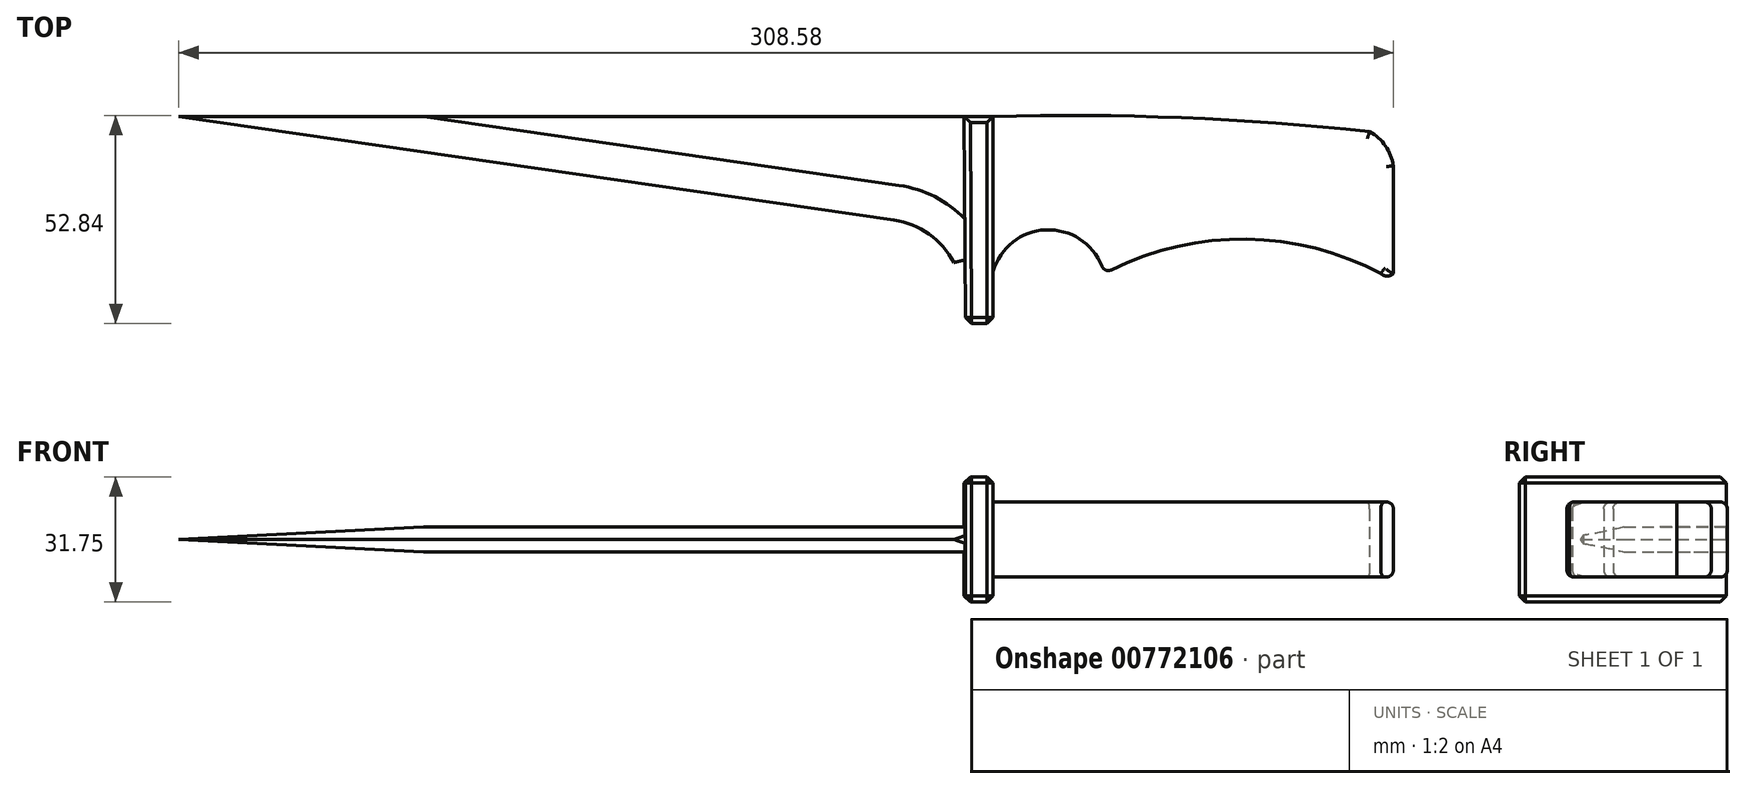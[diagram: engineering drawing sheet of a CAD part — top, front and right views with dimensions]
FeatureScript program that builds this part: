
annotation { "Feature Type Name" : "Feature", "Feature Type Description" : "" }
export const myFeature = defineFeature(function(context is Context, id is Id, definition is map)
    precondition{}
    {
        {
            var Q0;
            Q0=qCreatedBy(makeId("Top.planeOp"),FACE);
            var sketch = newSketch(context, id + "F0", { "sketchPlane" : qUnion([Q0])});
            skPoint(sketch, "E0.middle", {"position": v(0, 0) * mm});
            skLineSegment(sketch, "E1", {"start": v(52.6, 26.27) * mm, "end": v(52.6, -26.27) * mm});
            skLineSegment(sketch, "E2", {"start": v(-154.3, 26.27) * mm, "end": v(27.43, 0) * mm});
            skArc(sketch, "E3", {"start": v(44.85, -18.26) * mm, "mid": v(39.3, -6.12) * mm, "end": v(27.43, 0) * mm});
            skLineSegment(sketch, "E4", {"start": v(44.85, -18.26) * mm, "end": v(45.63, -26.27) * mm});
            skArc(sketch, "E5", {"start": v(80.81, -13.56) * mm, "mid": v(66.92, -2.46) * mm, "end": v(52.6, -13) * mm});
            skArc(sketch, "E6", {"start": v(151.07, -13.56) * mm, "mid": v(115.94, -4.83) * mm, "end": v(80.81, -13.56) * mm});
            skArc(sketch, "E7", {"start": v(151.07, -13.56) * mm, "mid": v(152.68, -14.21) * mm, "end": v(154.3, -13.56) * mm});
            skLineSegment(sketch, "E8", {"start": v(-154.3, 26.27) * mm, "end": v(52.6, 26.27) * mm});
            skLineSegment(sketch, "E9", {"start": v(45.63, -26.27) * mm, "end": v(52.6, -26.27) * mm});
            skArc(sketch, "E10", {"start": v(154.3, 13.76) * mm, "mid": v(152.29, 18.84) * mm, "end": v(148.23, 22.49) * mm});
            skArc(sketch, "E11", {"start": v(148.23, 22.49) * mm, "mid": v(100.48, 26.03) * mm, "end": v(52.6, 26.27) * mm});
            skLineSegment(sketch, "E12", {"start": v(154.3, 13.76) * mm, "end": v(154.3, -13.56) * mm});
            skLineSegment(sketch, "E13", {"start": v(45.63, -26.27) * mm, "end": v(45.24, 26.27) * mm});
            skPoint(sketch, "E13.endSnap0", {"position": v(45.24, -22.27) * mm});
            skSolve(sketch);
        }
        {
            var Q0;
            {var subQ1=sQuery(id+"F0.wireOp",EDGE,"E2");Q0=makeQuery(id+"F0.imprint","IMPRINT",FACE,{"disambiguationData":[TD([[makeQuery(id+"F0.imprint","IMPRINT",EDGE,{"derivedFrom":subQ1}),1.0]])]});}
            extrude(context, id + "F1", {"entities" : qUnion([Q0]), "depth" : 6.35 * mm, "offsetDistance" : 25.4 * mm});
        }
        {
            var Q0;
            {var subQ0=sQuery(id+"F0.wireOp",EDGE,"E5");Q0=makeQuery(id+"F0.imprint","IMPRINT",FACE,{"disambiguationData":[TD([[makeQuery(id+"F0.imprint","IMPRINT",EDGE,{"derivedFrom":subQ0}),-1.0]])]});}
            extrude(context, id + "F2", {"entities" : qUnion([Q0]), "depth" : 19.05 * mm, "offsetDistance" : 25.4 * mm});
        }
        {
            var Q0;
            Q0=makeQuery(id+"F1.opExtrude","SWEPT_BODY",BODY,{"disambiguationData":[OSD([sQuery(id+"F0.wireOp",EDGE,"E2"),sQuery(id+"F0.wireOp",EDGE,"E3"),sQuery(id+"F0.wireOp",EDGE,"E4"),sQuery(id+"F0.wireOp",EDGE,"E8"),sQuery(id+"F0.wireOp",EDGE,"E13")])]});
            transform(context, id + "F3", {"entities" : qUnion([Q0]), "transformType" : TransformType.TRANSLATION_3D, "dx" : 0 * mm, "dy" : 0 * mm, "dz" : 6.35 * mm, "makeCopy" : false});
        }
        {
            var Q0;
            Q0=makeQuery(id+"F2.opExtrude","SWEPT_BODY",BODY,{"disambiguationData":[OSD([sQuery(id+"F0.wireOp",EDGE,"E1"),sQuery(id+"F0.wireOp",EDGE,"E5"),sQuery(id+"F0.wireOp",EDGE,"E6"),sQuery(id+"F0.wireOp",EDGE,"E7"),sQuery(id+"F0.wireOp",EDGE,"E10"),sQuery(id+"F0.wireOp",EDGE,"E11"),sQuery(id+"F0.wireOp",EDGE,"E12")])]});
            transform(context, id + "F4", {"entities" : qUnion([Q0]), "transformType" : TransformType.TRANSLATION_3D, "dx" : 0 * mm, "dy" : 0 * mm, "dz" : 6.35 * mm, "makeCopy" : false});
        }
        {
            var Q0;
            Q0=makeQuery(id+"F1.opExtrude","SWEPT_BODY",BODY,{"disambiguationData":[OSD([sQuery(id+"F0.wireOp",EDGE,"E2"),sQuery(id+"F0.wireOp",EDGE,"E3"),sQuery(id+"F0.wireOp",EDGE,"E4"),sQuery(id+"F0.wireOp",EDGE,"E8"),sQuery(id+"F0.wireOp",EDGE,"E13")])]});
            transform(context, id + "F5", {"entities" : qUnion([Q0]), "transformType" : TransformType.TRANSLATION_3D, "dx" : 0 * mm, "dy" : 0 * mm, "dz" : 6.35 * mm, "makeCopy" : false});
        }
        {
            var Q0;
            {var subQ4=sQuery(id+"F0.wireOp",EDGE,"E9");Q0=makeQuery(id+"F0.imprint","IMPRINT",FACE,{"disambiguationData":[TD([[makeQuery(id+"F0.imprint","IMPRINT",EDGE,{"derivedFrom":subQ4}),1.0]])]});}
            extrude(context, id + "F6", {"entities" : qUnion([Q0]), "depth" : 31.75 * mm, "offsetDistance" : 25.4 * mm});
        }
        {
            var Q0;
            Q0=makeQuery(id+"F6.opExtrude","SWEPT_EDGE",EDGE,{"disambiguationData":[OSD([sQuery(id+"F0.wireOp",EDGE,"E4"),sQuery(id+"F0.wireOp",EDGE,"E9"),sQuery(id+"F0.wireOp",EDGE,"E13")])]});
            var Q1;
            Q1=makeQuery(id+"F6.opExtrude","SWEPT_EDGE",EDGE,{"disambiguationData":[OSD([sQuery(id+"F0.wireOp",EDGE,"E1"),sQuery(id+"F0.wireOp",EDGE,"E9")])]});
            var Q2;
            Q2=makeQuery(id+"F6.opExtrude","CAP_EDGE",EDGE,{"disambiguationData":[OSD([sQuery(id+"F0.wireOp",EDGE,"E13")])],"isStart":false});
            var Q3;
            Q3=makeQuery(id+"F6.opExtrude","CAP_EDGE",EDGE,{"disambiguationData":[OSD([sQuery(id+"F0.wireOp",EDGE,"E1")])],"isStart":false});
            var Q4;
            Q4=makeQuery(id+"F6.opExtrude","CAP_EDGE",EDGE,{"disambiguationData":[OSD([sQuery(id+"F0.wireOp",EDGE,"E13")])],"isStart":true});
            var Q5;
            Q5=makeQuery(id+"F6.opExtrude","CAP_EDGE",EDGE,{"disambiguationData":[OSD([sQuery(id+"F0.wireOp",EDGE,"E1")])],"isStart":true});
            var Q6;
            Q6=makeQuery(id+"F6.opExtrude","CAP_EDGE",EDGE,{"disambiguationData":[OSD([sQuery(id+"F0.wireOp",EDGE,"E9")])],"isStart":false});
            var Q7;
            Q7=makeQuery(id+"F6.opExtrude","CAP_EDGE",EDGE,{"disambiguationData":[OSD([sQuery(id+"F0.wireOp",EDGE,"E9")])],"isStart":true});
            var Q8;
            Q8=makeQuery(id+"F6.opExtrude","CAP_EDGE",EDGE,{"disambiguationData":[OSD([sQuery(id+"F0.wireOp",EDGE,"E8")])],"isStart":true});
            var Q9;
            Q9=makeQuery(id+"F6.opExtrude","CAP_EDGE",EDGE,{"disambiguationData":[OSD([sQuery(id+"F0.wireOp",EDGE,"E8")])],"isStart":false});
            var Q10;
            Q10=makeQuery(id+"F1.opExtrude","SWEPT_EDGE",EDGE,{"disambiguationData":[OSD([sQuery(id+"F0.wireOp",EDGE,"E4"),sQuery(id+"F0.wireOp",EDGE,"E9"),sQuery(id+"F0.wireOp",EDGE,"E13")])]});
            chamfer(context, id + "F7", {"entities" : qUnion([Q0, Q1, Q2, Q3, Q4, Q5, Q6, Q7, Q8, Q9, Q10]), "width" : 1.52 * mm, "tangentPropagation" : true});
        }
        {
            var Q0;
            Q0=makeQuery(id+"F1.opExtrude","CAP_EDGE",EDGE,{"disambiguationData":[OSD([sQuery(id+"F0.wireOp",EDGE,"E2")])],"isStart":false});
            var Q1;
            Q1=makeQuery(id+"F1.opExtrude","CAP_EDGE",EDGE,{"disambiguationData":[OSD([sQuery(id+"F0.wireOp",EDGE,"E3")])],"isStart":false});
            var Q2;
            Q2=makeQuery(id+"F1.opExtrude","CAP_EDGE",EDGE,{"disambiguationData":[OSD([sQuery(id+"F0.wireOp",EDGE,"E2")])],"isStart":true});
            var Q3;
            Q3=makeQuery(id+"F1.opExtrude","CAP_EDGE",EDGE,{"disambiguationData":[OSD([sQuery(id+"F0.wireOp",EDGE,"E3")])],"isStart":true});
            chamfer(context, id + "F8", {"entities" : qUnion([Q0, Q1, Q2, Q3]), "chamferType" : ChamferType.TWO_OFFSETS, "width1" : 8.9 * mm, "oppositeDirection" : false, "width2" : 3.17 * mm, "tangentPropagation" : true});
        }
        {
            var Q0;
            Q0=makeQuery(id+"F2.opExtrude","CAP_EDGE",EDGE,{"disambiguationData":[OSD([sQuery(id+"F0.wireOp",EDGE,"E5")])],"isStart":true});
            var Q1;
            Q1=makeQuery(id+"F2.opExtrude","CAP_EDGE",EDGE,{"disambiguationData":[OSD([sQuery(id+"F0.wireOp",EDGE,"E5")])],"isStart":false});
            var Q2;
            Q2=makeQuery(id+"F2.opExtrude","CAP_EDGE",EDGE,{"disambiguationData":[OSD([sQuery(id+"F0.wireOp",EDGE,"E6")])],"isStart":false});
            var Q3;
            Q3=makeQuery(id+"F2.opExtrude","CAP_EDGE",EDGE,{"disambiguationData":[OSD([sQuery(id+"F0.wireOp",EDGE,"E6")])],"isStart":true});
            var Q4;
            Q4=makeQuery(id+"F2.opExtrude","CAP_EDGE",EDGE,{"disambiguationData":[OSD([sQuery(id+"F0.wireOp",EDGE,"E11")])],"isStart":false});
            var Q5;
            Q5=makeQuery(id+"F2.opExtrude","CAP_EDGE",EDGE,{"disambiguationData":[OSD([sQuery(id+"F0.wireOp",EDGE,"E11")])],"isStart":true});
            var Q6;
            Q6=makeQuery(id+"F2.opExtrude","CAP_EDGE",EDGE,{"disambiguationData":[OSD([sQuery(id+"F0.wireOp",EDGE,"E10")])],"isStart":true});
            var Q7;
            Q7=makeQuery(id+"F2.opExtrude","CAP_EDGE",EDGE,{"disambiguationData":[OSD([sQuery(id+"F0.wireOp",EDGE,"E10")])],"isStart":false});
            var Q8;
            Q8=makeQuery(id+"F2.opExtrude","CAP_EDGE",EDGE,{"disambiguationData":[OSD([sQuery(id+"F0.wireOp",EDGE,"E12")])],"isStart":false});
            var Q9;
            Q9=makeQuery(id+"F2.opExtrude","CAP_EDGE",EDGE,{"disambiguationData":[OSD([sQuery(id+"F0.wireOp",EDGE,"E12")])],"isStart":true});
            var Q10;
            Q10=makeQuery(id+"F2.opExtrude","CAP_EDGE",EDGE,{"disambiguationData":[OSD([sQuery(id+"F0.wireOp",EDGE,"E7")])],"isStart":true});
            var Q11;
            Q11=makeQuery(id+"F2.opExtrude","CAP_EDGE",EDGE,{"disambiguationData":[OSD([sQuery(id+"F0.wireOp",EDGE,"E7")])],"isStart":false});
            var Q12;
            Q12=makeQuery(id+"F2.opExtrude","SWEPT_EDGE",EDGE,{"disambiguationData":[OSD([sQuery(id+"F0.wireOp",EDGE,"E5"),sQuery(id+"F0.wireOp",EDGE,"E6")])]});
            fillet(context, id + "F9", {"entities" : qUnion([Q0, Q1, Q2, Q3, Q4, Q5, Q6, Q7, Q8, Q9, Q10, Q11, Q12]), "radius" : 1.78 * mm, "tangentPropagation" : true, "allowEdgeOverflow" : false});
        }
    });
